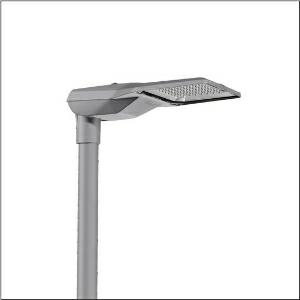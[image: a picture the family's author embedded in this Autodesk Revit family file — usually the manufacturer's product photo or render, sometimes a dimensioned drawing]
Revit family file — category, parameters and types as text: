
# Revit family: streetlight_sl_21_midi___st0_5a_5xe3b43s08lb_de93
name_source: partatom
category: Lighting Fixtures
units: mm (PartAtom-declared; Revit-internal decimal feet)

## family parameters
Cut with Voids When Loaded = No
Host = Face
Light Source = No
Part Type = Normal
Room Calculation Point = No
Round Connector Dimension = Use Diameter
Shared = No

## types (1)
- --- (1 x LED, 14950 lm, 99.6 W, 4000K)
    Apparent Load = 100 VA
    CIE Flux Codes = 41 75 97 100 100
    Color Rendering = 70
    Color Temperature = 4000K
    Default Elevation = 1800 mm
    Description = Streetlight SL 21 midi, mast luminaire, primary light control with lens, of PMMA, primary optical cover: cover, of toughened safety glass, transparent, light distribution: ST0.5a, light emission: direct distribution, primary light characteristic: asymmetric, installation type: side-entry, post-top, LED, High Power LED, rated luminous flux: 14.950lm, luminous efficacy: 150lm/W, light colour: 740, colour temperature: 4000K, control gear: D4i, control: overheat protection, constant luminous flux control, time-dependent luminous flux control, flexible luminous flux parameterisation, pre-setting: logarithmic dimming characteristic, mains connection: 230..240V, AC, 50/60Hz, start of lifetime: 100W, end of service life: 102W, reduction: 46W, luminaire housing, of diecast aluminium, powder-coated, Siteco® metallic grey (DB 702S), corrosivity category C5 mid according to DIN EN ISO 12944, please order mast flange separately, inclination adjustable: 0°, 5°, 10°, 15°, sealing non-destructively replaceable, multi-level sealing system, length: 644mm, width: 335mm, height: 110mm, mast flange for spigot size: 42mm (side-entry): 5XC10008XM4, 60/48mm (side-entry/post-top): 5XC10108XM2, 76/60mm (side-entry/post-top): 5XC10108XM1, mounting height: 4..8m, Smart Interface above, protection rating (complete): IP66, insulation class (complete): insulation class II (safety insulation), certification: CE, ENEC, ENEC+, VDE, impact resistance: IK10, permissible operating ambient temperature for outdoor applications: -40..+50°C, standard-compliant lighting for roads and squares, packaging unit: 1 piece

Light Distribution: ST0.5a
    Height = 111 mm
    Lamp = 1 x LED
    Lamp Light Flux = 14950 lm
    Lamp Power = 99.6 W
    Lamp count = 1
    Length = 644 mm
    Luminous efficacy = 150 lm/W
    Manufacturer = Siteco
    ModVariant = No
    Model = 5XE3B43S08LB
    Number of Poles = 1
    OnlyDefault = Yes
    Power Factor = 1
    Product Name = Streetlight SL 21 midi | ST0.5a
    Product group = mast luminaire | pylon top
    ProductGroupID = 6100
    Protection Class = Protection class II
    Protection Degree = IP 66
    RLX_Detail_Level = 1
    RLX_Emergency_Light_Flux = 0 lm
    RLX_Emergency_Type = 0
    RLX_Emergency_Type_DB = No
    RlxData = <blob elided: 37805 chars, md5=8e453922>
    Socket = socket
    Standby Power = 0 W
    System Light Flux = 14950 lm
    System Power = 100 W
    Type Comments = factory setting: luminous flux: 100 % | dim-lin: 254 | 1020 mA
    Type Image = l_1004302.jpg
    URL = http://relux.com
    VarID = @adj_032579
    Voltage = 0 V
    Weight = 0.00 kg
    Width = 336 mm

## geometry (parser evidence)
native form markers: Blend x4, Sweep x11
no freeform markers — native parametric forms only
